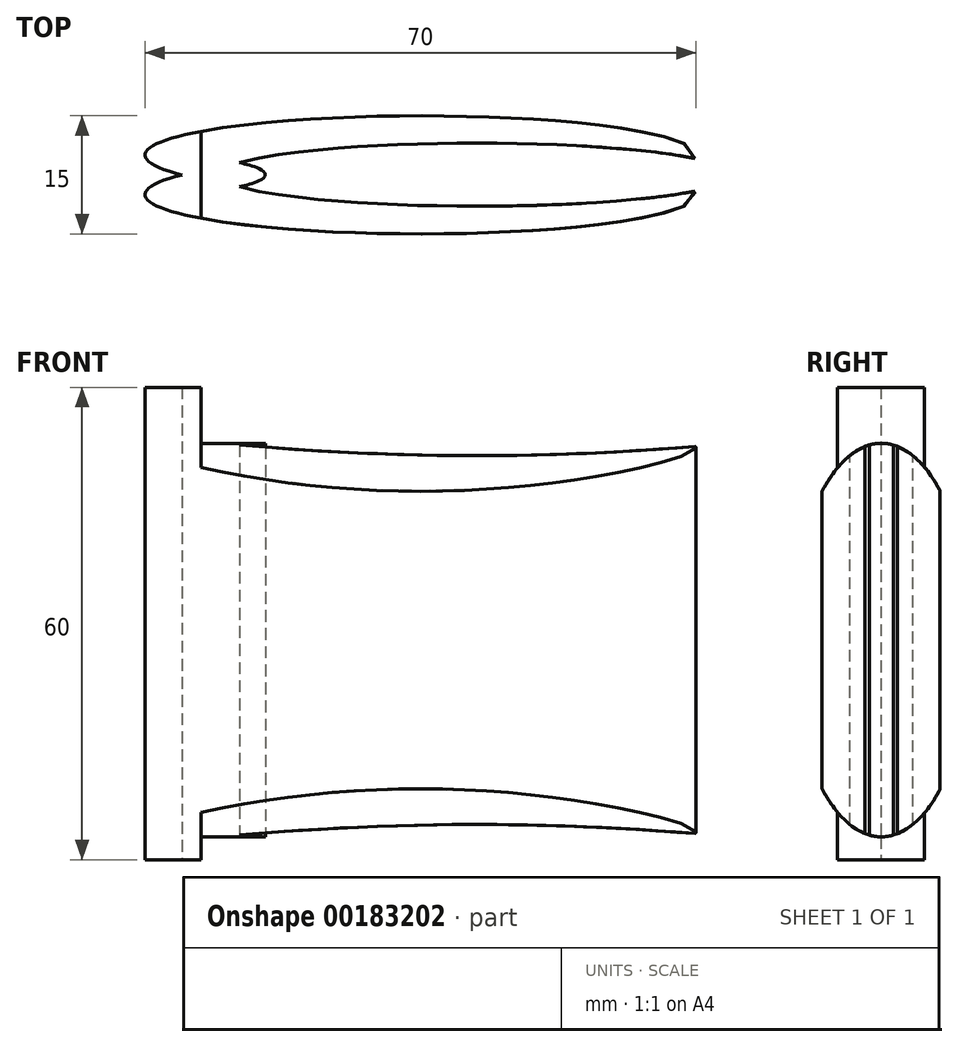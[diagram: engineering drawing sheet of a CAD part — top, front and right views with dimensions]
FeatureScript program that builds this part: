
annotation { "Feature Type Name" : "Feature", "Feature Type Description" : "" }
export const myFeature = defineFeature(function(context is Context, id is Id, definition is map)
    precondition{}
    {
        {
            var Q0;
            Q0=qCreatedBy(makeId("Top.planeOp"),FACE);
            var sketch = newSketch(context, id + "F0", { "sketchPlane" : qUnion([Q0])});
            skEllipticalArc(sketch, "E0", {});
            skEllipticalArc(sketch, "E1", {});
            skEllipticalArc(sketch, "E2", {});
            skEllipticalArc(sketch, "E3", {});
            const initialGuessF0  = {"E0": [0, 0, -1, 0, 0.0325, 0.004, 0.38989282119353114, 5.893292485986053], "E1": [-0.0071032149717211775, 0.002482675826177002, -1, 0, 0.035, 0.005, 0.8792265867573081, 0.5235987755982995], "E2": [-0.007103214971721178, -0.002517324173822999, -1, 0, 0.035, 0.005, 5.759586531581287, 5.400525675045287], "E3": [-0.07489510625600815, 0, 1, 0, 0.048094406723976135, 0.004200928842927729, 5.912869601259555, 0.3703157059200302]};
            skSetInitialGuess(sketch, initialGuessF0);
            skSolve(sketch);
        }
        {
            var Q0;
            {var subQ0=sQuery(id+"F0.wireOp",EDGE,"E2");var subQ1=sQuery(id+"F0.wireOp",EDGE,"E0");var subQ2=makeQuery(id+"F0.imprint","INTERSECT",VERTEX,{"disambiguationData":[OD(0.0)],"derivedFrom":[subQ1,subQ0]});Q0=makeQuery(id+"F0.imprint","IMPRINT",FACE,{"disambiguationData":[TD([[makeQuery(id+"F0.imprint","IMPRINT",EDGE,{"disambiguationData":[TD([[subQ2,1.0]])],"derivedFrom":subQ1}),-1.0]])]});}
            var Q1;
            {var subQ0=sQuery(id+"F0.wireOp",EDGE,"E1");var subQ1=sQuery(id+"F0.wireOp",EDGE,"E0");var subQ2=makeQuery(id+"F0.imprint","INTERSECT",VERTEX,{"disambiguationData":[OD(0.0)],"derivedFrom":[subQ1,subQ0]});Q1=makeQuery(id+"F0.imprint","IMPRINT",FACE,{"disambiguationData":[TD([[makeQuery(id+"F0.imprint","IMPRINT",EDGE,{"disambiguationData":[TD([[subQ2,-1.0]])],"derivedFrom":subQ1}),-1.0]])]});}
            var Q2;
            {var subQ0=sQuery(id+"F0.wireOp",EDGE,"E1");var subQ1=sQuery(id+"F0.wireOp",EDGE,"E0");var subQ2=makeQuery(id+"F0.imprint","INTERSECT",VERTEX,{"disambiguationData":[OD(1.0)],"derivedFrom":[subQ1,subQ0]});Q2=makeQuery(id+"F0.imprint","IMPRINT",FACE,{"disambiguationData":[TD([[makeQuery(id+"F0.imprint","IMPRINT",EDGE,{"disambiguationData":[TD([[subQ2,1.0]])],"derivedFrom":subQ1}),-1.0]])]});}
            var Q3;
            Q3 = qSketchRegion(id + "F2", true);
            extrude(context, id + "F1", {"entities" : qUnion([Q0, Q1, Q2, Q3]), "depth" : 60 * mm});
        }
        {
            var Q0;
            Q0=qCreatedBy(makeId("Front.planeOp"),FACE);
            var sketch = newSketch(context, id + "F2", { "sketchPlane" : qUnion([Q0])});
            skLineSegment(sketch, "E4.bottom", {"start": v(76, 70.3) * mm, "end": v(-91.97, 70.3) * mm});
            skLineSegment(sketch, "E4.top", {"start": v(76, -18.72) * mm, "end": v(-91.97, -18.72) * mm});
            skLineSegment(sketch, "E4.left", {"start": v(76, 70.3) * mm, "end": v(76, -18.72) * mm});
            skLineSegment(sketch, "E4.right", {"start": v(-91.97, 70.3) * mm, "end": v(-91.97, -18.72) * mm});
            skLineSegment(sketch, "E5", {"start": v(-61.49, 39.66) * mm, "end": v(-61.6, 39.69) * mm});
            skPoint(sketch, "E6.trimOffspring.end.orphan", {"position": v(-100.69, 0) * mm});
            skLineSegment(sketch, "E7", {"start": v(-71.82, 34.51) * mm, "end": v(49.88, 65.17) * mm});
            skLineSegment(sketch, "E8.0", {"start": v(-63.88, 3) * mm, "end": v(57.82, 33.65) * mm});
            skLineSegment(sketch, "E9", {"start": v(-71.82, 34.51) * mm, "end": v(-63.88, 3) * mm});
            skLineSegment(sketch, "E10", {"start": v(49.88, 65.17) * mm, "end": v(57.82, 33.65) * mm});
            skSolve(sketch);
        }
        {
            var Q0;
            Q0=qCreatedBy(makeId("Right.planeOp"),FACE);
            var sketch = newSketch(context, id + "F3", { "sketchPlane" : qUnion([Q0])});
            skEllipse(sketch, "E11", {"center": v(0, 27.9) * mm, "majorRadius": 25 * mm, "minorRadius": 11.48 * mm, "majorAxis": v(0, 1)});
            skLineSegment(sketch, "E12.bottom", {"start": v(33.4, 65.08) * mm, "end": v(-43.9, 65.08) * mm});
            skLineSegment(sketch, "E12.top", {"start": v(33.4, -13.74) * mm, "end": v(-43.9, -13.74) * mm});
            skLineSegment(sketch, "E12.left", {"start": v(33.4, 65.08) * mm, "end": v(33.4, -13.74) * mm});
            skLineSegment(sketch, "E12.right", {"start": v(-43.9, 65.08) * mm, "end": v(-43.9, -13.74) * mm});
            skSolve(sketch);
        }
        {
            var Q0;
            Q0=makeQuery(id+"F3.imprint","IMPRINT",FACE,{"disambiguationData":[TD([[makeQuery(id+"F3.imprint","IMPRINT",EDGE,{"derivedFrom":sQuery(id+"F3.wireOp",EDGE,"E11")}),-1.0]])]});
            extrude(context, id + "F4", {"entities" : qUnion([Q0]), "operationType" : NewBodyOperationType.REMOVE, "endBound" : BoundingType.SYMMETRIC, "oppositeDirection" : true, "depth" : 70 * mm});
        }
    });
